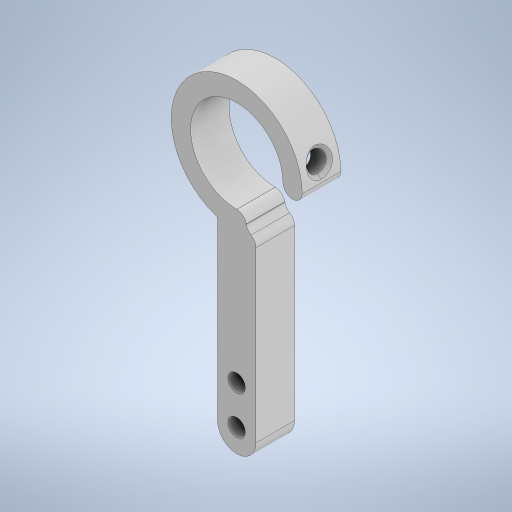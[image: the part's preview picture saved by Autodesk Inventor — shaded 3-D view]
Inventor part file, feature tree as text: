
AUTODESK INVENTOR PART (.ipt)
format: ipt  version: 2023 (Build 270158000, 158)  size: 316,416 bytes
history: native  units: mm
features: sketch x3, extrude x2, fillet x2, other x1, revolve x1, chamfer x1
ambient origin geometry x8: Origin, YZ Plane, XZ Plane, XY Plane, X Axis, Y Axis, Z Axis, Center Point
bodies: Body1 (feature_tree)
feature tree (10):
  other  "솔리드1"
  extrude  "돌출1"  Depth=10.0mm
  fillet  "모깎기1"  Radius=55.0mm
  revolve  "회전1"
  chamfer  "모따기1"  Distance=24.0mm
  extrude  "돌출2"  Depth=34.0mm
  fillet  "모깎기2"  Radius=10.0mm
  sketch  "스케치1"
  sketch  "스케치2"
  sketch  "스케치3"
